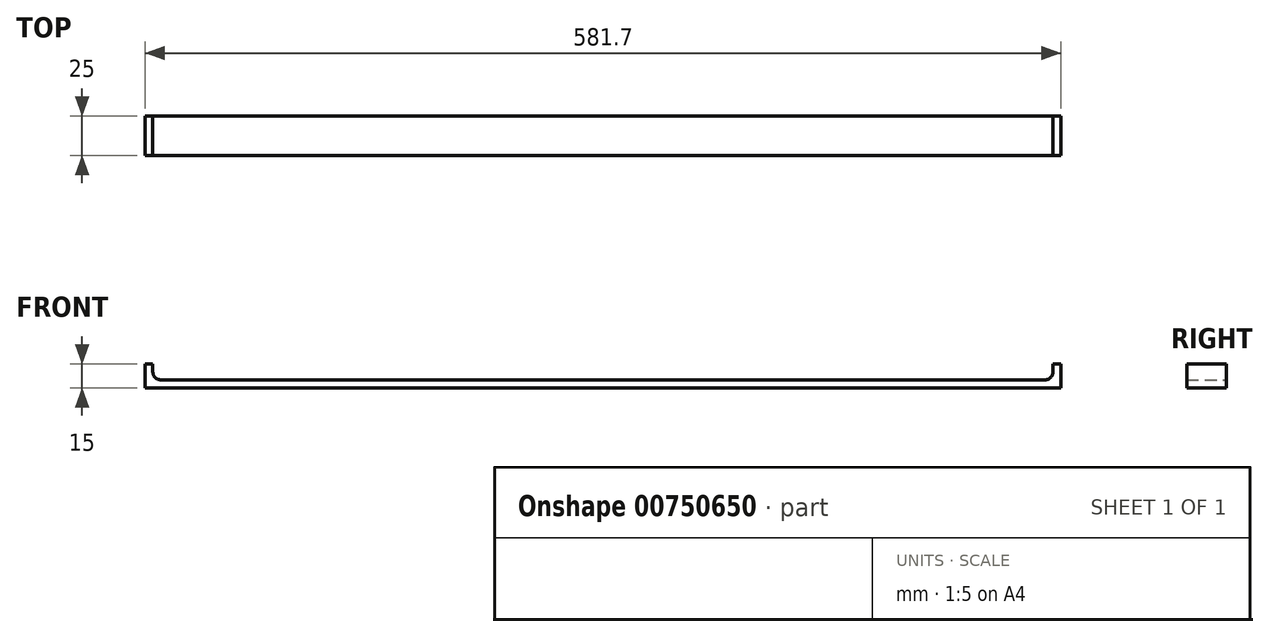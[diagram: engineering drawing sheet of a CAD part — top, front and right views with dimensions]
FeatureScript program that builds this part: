
annotation { "Feature Type Name" : "Feature", "Feature Type Description" : "" }
export const myFeature = defineFeature(function(context is Context, id is Id, definition is map)
    precondition{}
    {
        {
            var Q0;
            Q0=qCreatedBy(makeId("Front.planeOp"),FACE);
            var sketch = newSketch(context, id + "F0", { "sketchPlane" : qUnion([Q0])});
            skArc(sketch, "E0", {"start": v(-68.54, 2.4) * mm, "mid": v(-67.08, -1.15) * mm, "end": v(-63.54, -2.6) * mm});
            skArc(sketch, "E1", {"start": v(498.16, -2.6) * mm, "mid": v(501.7, -1.15) * mm, "end": v(503.16, 2.4) * mm});
            skLineSegment(sketch, "E2", {"start": v(-68.54, -7.6) * mm, "end": v(503.16, -7.6) * mm});
            skLineSegment(sketch, "E3", {"start": v(498.16, -2.6) * mm, "end": v(-63.54, -2.6) * mm});
            skLineSegment(sketch, "E4", {"start": v(-68.54, -7.6) * mm, "end": v(-73.54, -7.6) * mm});
            skLineSegment(sketch, "E5", {"start": v(-73.54, -7.6) * mm, "end": v(-73.54, 7.4) * mm});
            skLineSegment(sketch, "E6", {"start": v(-73.54, 7.4) * mm, "end": v(-68.54, 7.4) * mm});
            skLineSegment(sketch, "E7", {"start": v(-68.54, 7.4) * mm, "end": v(-68.54, 2.4) * mm});
            skLineSegment(sketch, "E8", {"start": v(503.16, -7.6) * mm, "end": v(508.16, -7.6) * mm});
            skLineSegment(sketch, "E9", {"start": v(508.16, -7.6) * mm, "end": v(508.16, 7.4) * mm});
            skLineSegment(sketch, "E10", {"start": v(508.16, 7.4) * mm, "end": v(503.16, 7.4) * mm});
            skLineSegment(sketch, "E11", {"start": v(503.16, 7.4) * mm, "end": v(503.16, 2.4) * mm});
            skSolve(sketch);
        }
        {
            var Q0;
            Q0 = qSketchRegion(id + "F0", true);
            extrude(context, id + "F1", {"entities" : qUnion([Q0]), "depth" : 25 * mm, "offsetDistance" : 25 * mm});
        }
    });
